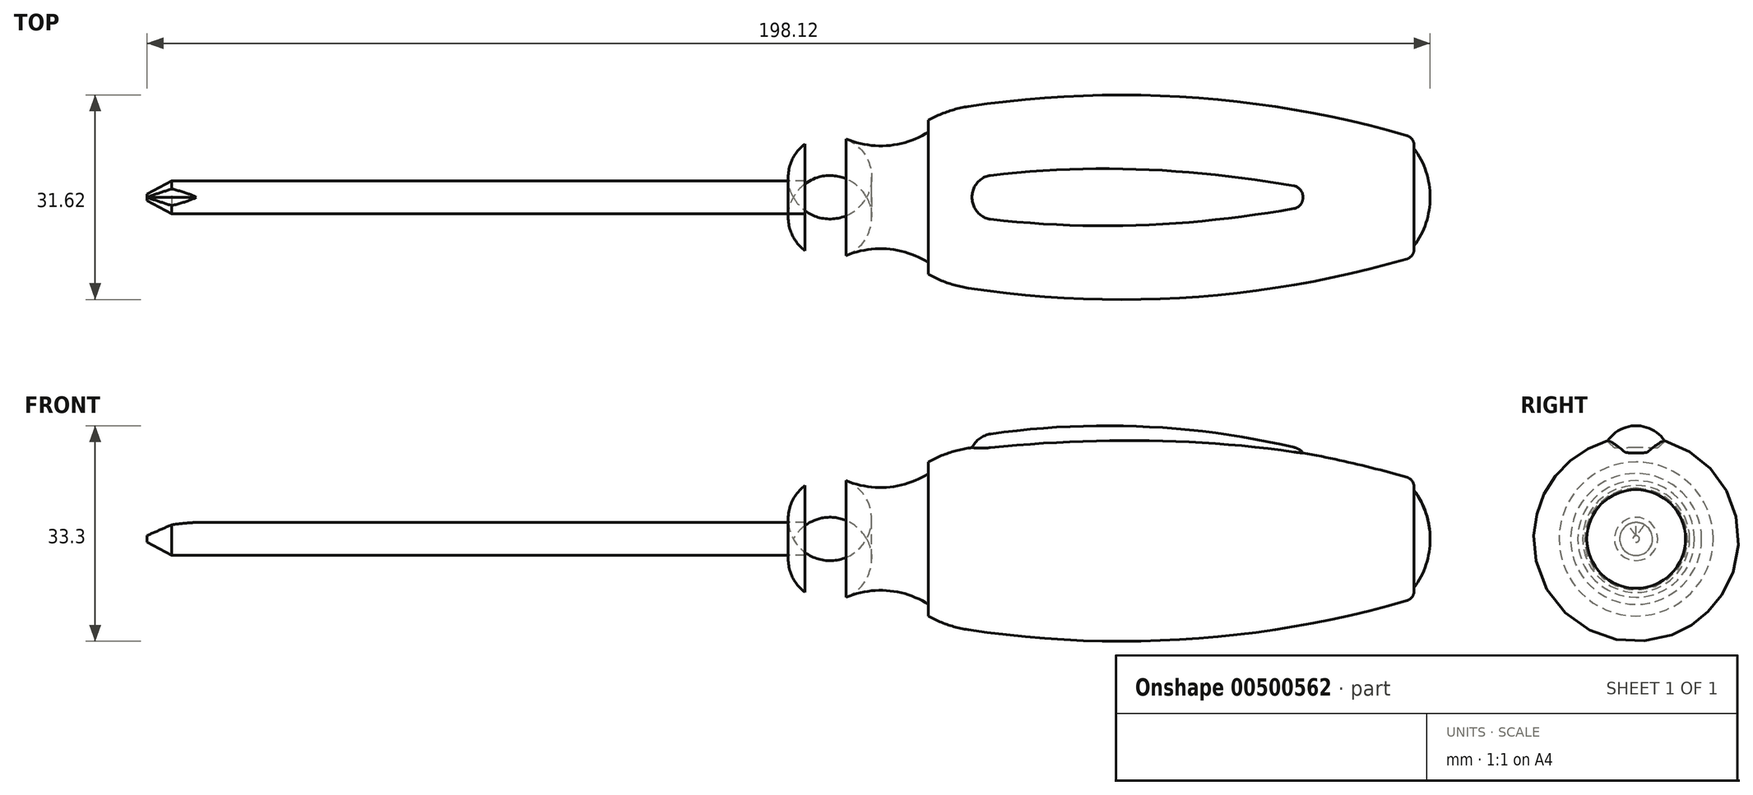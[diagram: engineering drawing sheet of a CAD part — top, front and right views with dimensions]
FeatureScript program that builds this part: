
annotation { "Feature Type Name" : "Feature", "Feature Type Description" : "" }
export const myFeature = defineFeature(function(context is Context, id is Id, definition is map)
    precondition{}
    {
        {
            var Q0;
            Q0=qCreatedBy(makeId("Front.planeOp"),FACE);
            var sketch = newSketch(context, id + "F0", { "sketchPlane" : qUnion([Q0])});
            skLineSegment(sketch, "E0", {"start": v(-101.6, 0) * mm, "end": v(96.52, 0) * mm});
            skLineSegment(sketch, "E1", {"start": v(96.52, 0) * mm, "end": v(145.25, 0) * mm, "construction": true});
            skLineSegment(sketch, "E2", {"start": v(50.8, 2.54) * mm, "end": v(-97.8, 2.54) * mm});
            skLineSegment(sketch, "E3", {"start": v(-101.6, 0.5) * mm, "end": v(-101.6, 0) * mm});
            skLineSegment(sketch, "E4", {"start": v(0, 2.54) * mm, "end": v(0, 8.26) * mm});
            skArc(sketch, "E5", {"start": v(6.35, 9.02) * mm, "mid": v(3.07, 9.48) * mm, "end": v(0, 8.26) * mm});
            skArc(sketch, "E6", {"start": v(6.35, 9.02) * mm, "mid": v(12.84, 7.99) * mm, "end": v(19.05, 10.11) * mm});
            skArc(sketch, "E7", {"start": v(25.4, 12.52) * mm, "mid": v(22.1, 11.65) * mm, "end": v(19.05, 10.11) * mm});
            skArc(sketch, "E8", {"start": v(93.98, 7.62) * mm, "mid": v(59.96, 13.9) * mm, "end": v(25.4, 12.52) * mm});
            skArc(sketch, "E9", {"start": v(96.52, 0) * mm, "mid": v(95.87, 4.02) * mm, "end": v(93.98, 7.62) * mm});
            skArc(sketch, "E10.0", {"start": v(25.17, 14.02) * mm, "mid": v(22.01, 13.24) * mm, "end": v(19.05, 11.9) * mm});
            skArc(sketch, "E10.1", {"start": v(92.95, 9.52) * mm, "mid": v(59.3, 15.46) * mm, "end": v(25.17, 14.02) * mm});
            skLineSegment(sketch, "E11", {"start": v(19.05, 11.9) * mm, "end": v(19.05, 10.11) * mm});
            skArc(sketch, "E12", {"start": v(93.98, 7.62) * mm, "mid": v(93.86, 8.78) * mm, "end": v(92.95, 9.52) * mm});
            skPoint(sketch, "E13.orphan", {"position": v(0, 25.5) * mm});
            skLineSegment(sketch, "E14", {"start": v(50.8, 2.54) * mm, "end": v(50.8, 0) * mm});
            skLineSegment(sketch, "E15", {"start": v(-101.6, 0.5) * mm, "end": v(-97.8, 2.54) * mm});
            skPoint(sketch, "E16.orphan", {"position": v(-101.6, 2.54) * mm});
            skSolve(sketch);
        }
        {
            var Q0;
            Q0=qCreatedBy(makeId("Front.planeOp"),FACE);
            var sketch = newSketch(context, id + "F1", { "sketchPlane" : qUnion([Q0])});
            skLineSegment(sketch, "E17", {"start": v(25.4, 12.52) * mm, "end": v(77.47, 11.64) * mm});
            skArc(sketch, "E18", {"start": v(28.67, 16.22) * mm, "mid": v(26.35, 14.97) * mm, "end": v(25.4, 12.52) * mm});
            skArc(sketch, "E19", {"start": v(77.47, 11.64) * mm, "mid": v(76.93, 13.25) * mm, "end": v(75.5, 14.16) * mm});
            skArc(sketch, "E20", {"start": v(75.5, 14.16) * mm, "mid": v(52.19, 17.37) * mm, "end": v(28.67, 16.22) * mm});
            skSolve(sketch);
        }
        {
            var Q0;
            Q0=qCreatedBy(makeId("Front.planeOp"),FACE);
            var sketch = newSketch(context, id + "F2", { "sketchPlane" : qUnion([Q0])});
            skLineSegment(sketch, "E21", {"start": v(-101.6, 0.5) * mm, "end": v(-93.98, 2.54) * mm});
            skSolve(sketch);
        }
        {
            var Q0;
            Q0=sQuery(id+"F2.wireOp",VERTEX,"E21.start");
            var Q1;
            Q1=sQuery(id+"F2.wireOp",EDGE,"E21");
            cPlane(context, id + "F3", {"entities" : qUnion([Q0, Q1]), "cplaneType" : CPlaneType.LINE_POINT, "offset" : 25.4 * mm, "width" : 152.4 * mm, "height" : 152.4 * mm});
        }
        {
            var Q0;
            Q0=qCreatedBy(id+"F3.planeOp",FACE);
            var sketch = newSketch(context, id + "F4", { "sketchPlane" : qUnion([Q0])});
            skLineSegment(sketch, "E22", {"start": v(5.08, 29.2) * mm, "end": v(0, 26.67) * mm});
            skLineSegment(sketch, "E23", {"start": v(0, 26.67) * mm, "end": v(-5.08, 29.2) * mm});
            skLineSegment(sketch, "E24", {"start": v(-5.08, 29.2) * mm, "end": v(5.08, 29.2) * mm});
            skLineSegment(sketch, "E25", {"start": v(0, 29.2) * mm, "end": v(0, 26.67) * mm, "construction": true});
            skSolve(sketch);
        }
        {
            var Q0;
            {var subQ0=sQuery(id+"F0.wireOp",EDGE,"E3");Q0=makeQuery(id+"F0.imprint","IMPRINT",FACE,{"disambiguationData":[TD([[makeQuery(id+"F0.imprint","IMPRINT",EDGE,{"derivedFrom":subQ0}),1.0]])]});}
            var Q1;
            Q1=sQuery(id+"F0.wireOp",EDGE,"E1");
            revolve(context, id + "F5", {"entities" : qUnion([Q0]), "axis" : qUnion([Q1]), "revolveType" : RevolveType.FULL});
        }
        {
            var Q0;
            {var subQ0=sQuery(id+"F0.wireOp",EDGE,"E4");Q0=makeQuery(id+"F0.imprint","IMPRINT",FACE,{"disambiguationData":[TD([[makeQuery(id+"F0.imprint","IMPRINT",EDGE,{"derivedFrom":subQ0}),-1.0]])]});}
            var Q1;
            Q1=sQuery(id+"F0.wireOp",EDGE,"E1");
            revolve(context, id + "F6", {"operationType" : NewBodyOperationType.ADD, "entities" : qUnion([Q0]), "axis" : qUnion([Q1]), "revolveType" : RevolveType.FULL});
        }
        {
            var Q0;
            Q0=makeQuery(id+"F0.imprint","IMPRINT",FACE,{"disambiguationData":[TD([[makeQuery(id+"F0.imprint","IMPRINT",EDGE,{"derivedFrom":sQuery(id+"F0.wireOp",EDGE,"E7")}),-1.0]])]});
            var Q1;
            Q1=sQuery(id+"F0.wireOp",EDGE,"E1");
            revolve(context, id + "F7", {"operationType" : NewBodyOperationType.ADD, "entities" : qUnion([Q0]), "axis" : qUnion([Q1]), "revolveType" : RevolveType.FULL});
        }
        {
            var Q0;
            Q0=makeQuery(id+"F1.imprint","IMPRINT",FACE,{"disambiguationData":[TD([[makeQuery(id+"F1.imprint","IMPRINT",EDGE,{"derivedFrom":sQuery(id+"F1.wireOp",EDGE,"E17")}),1.0]])]});
            var Q1;
            Q1=sQuery(id+"F1.wireOp",EDGE,"E17");
            revolve(context, id + "F8", {"operationType" : NewBodyOperationType.ADD, "entities" : qUnion([Q0]), "axis" : qUnion([Q1]), "revolveType" : RevolveType.FULL});
        }
        {
            var Q0;
            Q0=makeQuery(id+"F4.imprint","IMPRINT",FACE,{"disambiguationData":[TD([[makeQuery(id+"F4.imprint","IMPRINT",EDGE,{"derivedFrom":sQuery(id+"F4.wireOp",EDGE,"E22")}),-1.0]])]});
            var Q1;
            Q1=sQuery(id+"F2.wireOp",EDGE,"E21");
            sweep(context, id + "F9", {"operationType" : NewBodyOperationType.REMOVE, "profiles" : qUnion([Q0]), "path" : qUnion([Q1])});
        }
    });
